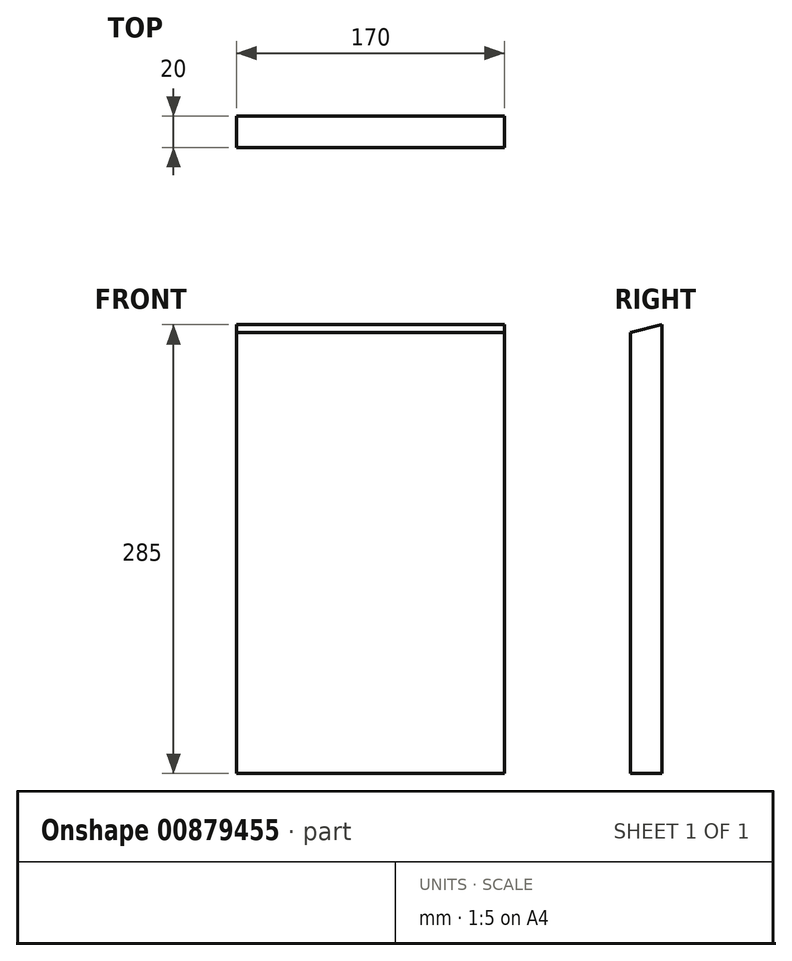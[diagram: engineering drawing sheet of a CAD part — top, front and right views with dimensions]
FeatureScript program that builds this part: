
annotation { "Feature Type Name" : "Feature", "Feature Type Description" : "" }
export const myFeature = defineFeature(function(context is Context, id is Id, definition is map)
    precondition{}
    {
        {
            var Q0;
            Q0=qCreatedBy(makeId("Top.planeOp"),FACE);
            var sketch = newSketch(context, id + "F0", { "sketchPlane" : qUnion([Q0])});
            skLineSegment(sketch, "E0.bottom", {"start": v(85, 142.5) * mm, "end": v(-85, 142.5) * mm});
            skLineSegment(sketch, "E0.top", {"start": v(85, -142.5) * mm, "end": v(-85, -142.5) * mm});
            skLineSegment(sketch, "E0.left", {"start": v(85, 142.5) * mm, "end": v(85, -142.5) * mm});
            skLineSegment(sketch, "E0.right", {"start": v(-85, 142.5) * mm, "end": v(-85, -142.5) * mm});
            skPoint(sketch, "E0.middle", {"position": v(0, 0) * mm});
            skSolve(sketch);
        }
        {
            var Q0;
            Q0=makeQuery(id+"F0.imprint","IMPRINT",FACE,{"disambiguationData":[TD([[makeQuery(id+"F0.imprint","IMPRINT",EDGE,{"derivedFrom":sQuery(id+"F0.wireOp",EDGE,"E0.bottom")}),1.0]])]});
            extrude(context, id + "F1", {"entities" : qUnion([Q0]), "endBound" : BoundingType.SYMMETRIC, "depth" : 20 * mm, "offsetDistance" : 25 * mm});
        }
        {
            var Q0;
            Q0=makeQuery(id+"F1.opExtrude","SWEPT_FACE",FACE,{"disambiguationData":[OSD([sQuery(id+"F0.wireOp",EDGE,"E0.right")])]});
            var sketch = newSketch(context, id + "F2", { "sketchPlane" : qUnion([Q0])});
            skPoint(sketch, "E1", {"position": v(-137.5, 10) * mm});
            skLineSegment(sketch, "E2", {"start": v(-137.5, 10) * mm, "end": v(-142.5, -10) * mm});
            skSolve(sketch);
        }
        {
            var Q0;
            Q0 = qSketchRegion(id + "F2", true);
            var Q1;
            {var subQ0=sQuery(id+"F2.wireOp",EDGE,"E2");Q1=makeQuery(id+"F2.imprint","IMPRINT",FACE,{"disambiguationData":[TD([[makeQuery(id+"F2.imprint","IMPRINT",EDGE,{"derivedFrom":subQ0}),-1.0]])]});}
            extrude(context, id + "F3", {"entities" : qUnion([Q0, Q1]), "operationType" : NewBodyOperationType.REMOVE, "endBound" : BoundingType.THROUGH_ALL, "oppositeDirection" : true, "depth" : 25 * mm, "offsetDistance" : 25 * mm});
        }
        {
            var Q0;
            Q0=qCreatedBy(makeId("Top.planeOp"),FACE);
            var sketch = newSketch(context, id + "F4", { "sketchPlane" : qUnion([Q0])});
            skLineSegment(sketch, "E3", {"start": v(0, 0) * mm, "end": v(133.74, 0) * mm, "construction": true});
            skSolve(sketch);
        }
        {
            var Q0;
            Q0=makeQuery(id+"F1.opExtrude","SWEPT_BODY",BODY,{"disambiguationData":[OSD([sQuery(id+"F0.wireOp",EDGE,"E0.bottom"),sQuery(id+"F0.wireOp",EDGE,"E0.top"),sQuery(id+"F0.wireOp",EDGE,"E0.left"),sQuery(id+"F0.wireOp",EDGE,"E0.right")])]});
            var Q1;
            Q1=sQuery(id+"F4.wireOp",EDGE,"E3");
            var Q2;
            Q2=sQuery(id+"F4.wireOp",EDGE,"E3");
            transform(context, id + "F5", {"entities" : qUnion([Q0]), "transformType" : TransformType.ROTATION, "transformAxis" : qUnion([Q2]), "angle" : 90 * degree, "makeCopy" : false});
        }
    });
